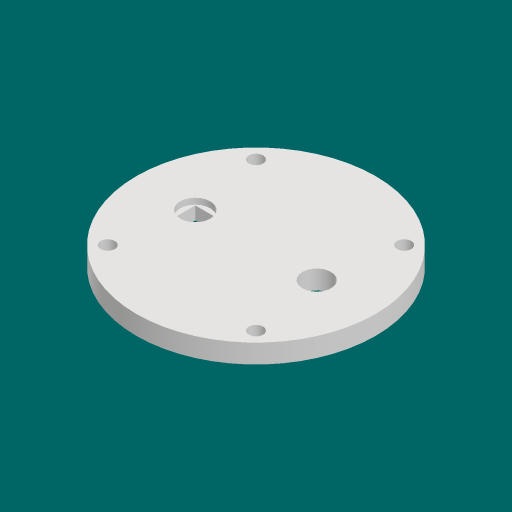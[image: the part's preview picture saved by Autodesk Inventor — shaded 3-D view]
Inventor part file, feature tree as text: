
AUTODESK INVENTOR PART (.ipt)
format: ipt  version: 2023.1 (Build 271208000, 208)  size: 131,072 bytes
history: native  units: in
note: dims shown in document units (in); Inventor stores cm internally (conversion verified against a paired STEP export)
features: sketch x3, extrude x2
ambient origin geometry x8: Origin, YZ Plane, XZ Plane, XY Plane, X Axis, Y Axis, Z Axis, Center Point
bodies: Solid1 (feature_tree)
feature tree (5):
  sketch  "Sketch1"  dims[d0=0.375in d1=3.1496in]
  extrude  "Extrusion1"  Depth=3.1496in
  extrude  "Extrusion2"  Depth=2.75in
  sketch  "Sketch2"  dims[d2=0.75in d3=2.75in]
  sketch  "Sketch3"  dims[d5=1.6in d6=3.2in d7=45.0deg d8=0.1875in d9=0.1in d10=1.5748in d12=360.0deg d14=0.25in d15=0.0in d16=0.261in d18=0.3957in d19=0.3957in d20=0.0787in d21=0.0in]
